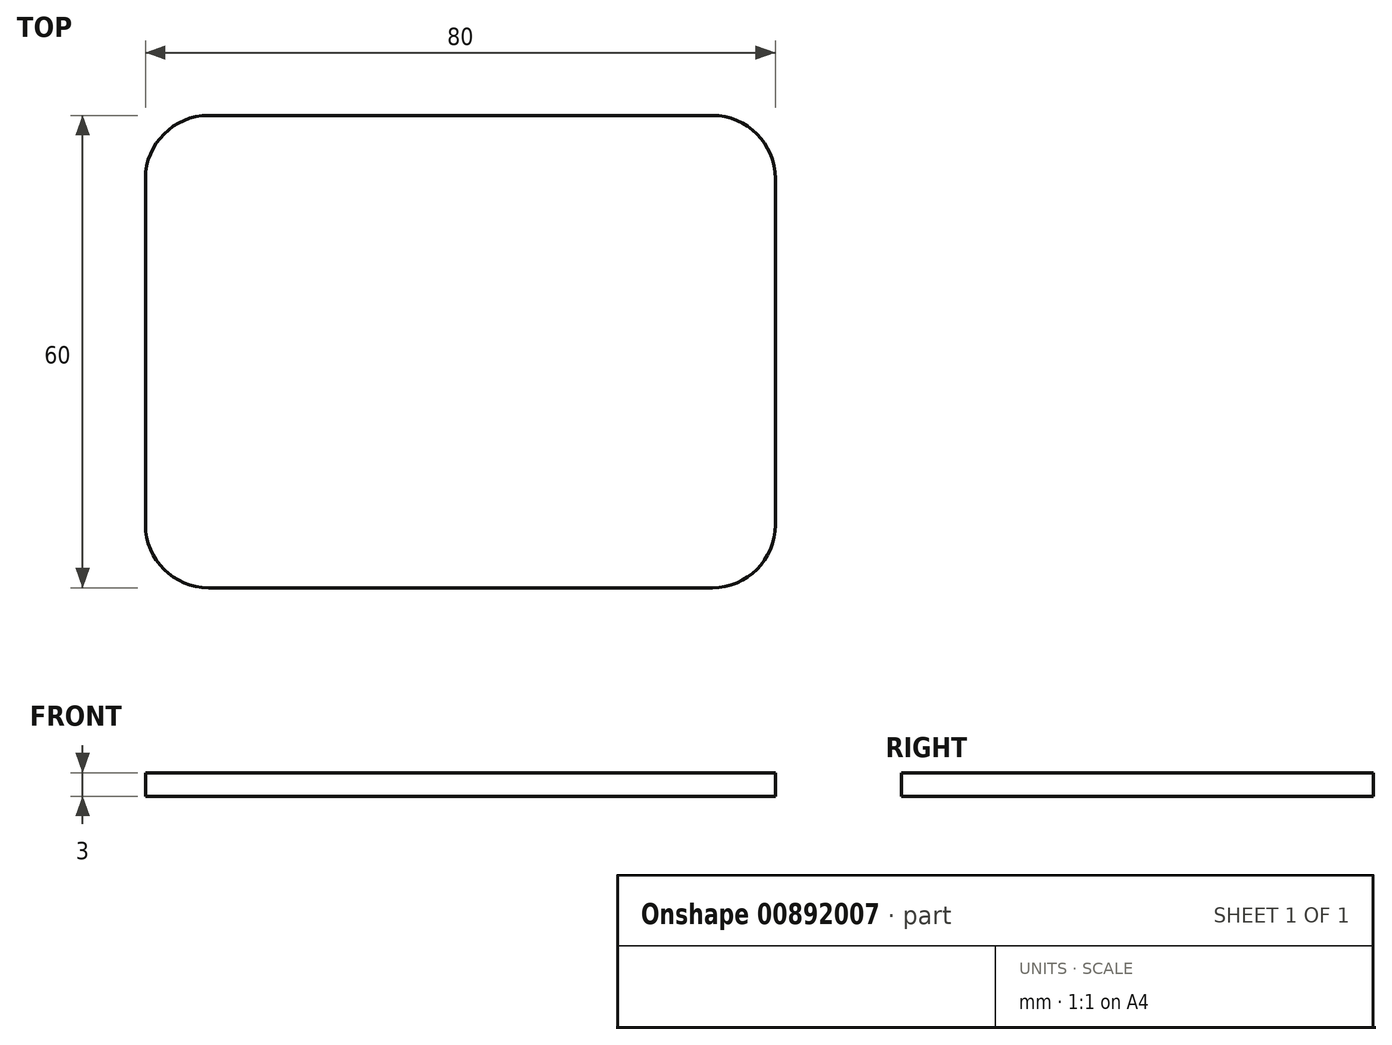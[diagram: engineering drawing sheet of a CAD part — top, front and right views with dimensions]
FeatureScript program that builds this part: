
annotation { "Feature Type Name" : "Feature", "Feature Type Description" : "" }
export const myFeature = defineFeature(function(context is Context, id is Id, definition is map)
    precondition{}
    {
        {
            var Q0;
            Q0=qCreatedBy(makeId("Top.planeOp"),FACE);
            var sketch = newSketch(context, id + "F0", { "sketchPlane" : qUnion([Q0])});
            skLineSegment(sketch, "E0.bottom", {"start": v(-32, 30) * mm, "end": v(32, 30) * mm});
            skLineSegment(sketch, "E0.top", {"start": v(-32, -30) * mm, "end": v(32, -30) * mm});
            skLineSegment(sketch, "E0.left", {"start": v(-40, 22) * mm, "end": v(-40, -22) * mm});
            skLineSegment(sketch, "E0.right", {"start": v(40, 22) * mm, "end": v(40, -22) * mm});
            skPoint(sketch, "E1.visualSharp", {"position": v(-40, 30) * mm});
            skArc(sketch, "E1.filletArc", {"start": v(-32, 30) * mm, "mid": v(-37.66, 27.66) * mm, "end": v(-40, 22) * mm});
            skPoint(sketch, "E2.visualSharp", {"position": v(40, 30) * mm});
            skArc(sketch, "E2.filletArc", {"start": v(40, 22) * mm, "mid": v(37.66, 27.66) * mm, "end": v(32, 30) * mm});
            skPoint(sketch, "E3.visualSharp", {"position": v(40, -30) * mm});
            skArc(sketch, "E3.filletArc", {"start": v(32, -30) * mm, "mid": v(37.66, -27.66) * mm, "end": v(40, -22) * mm});
            skPoint(sketch, "E4.visualSharp", {"position": v(-40, -30) * mm});
            skArc(sketch, "E4.filletArc", {"start": v(-40, -22) * mm, "mid": v(-37.66, -27.66) * mm, "end": v(-32, -30) * mm});
            skSolve(sketch);
        }
        {
            var Q0;
            Q0 = qSketchRegion(id + "F0", true);
            var Q1;
            Q1=makeQuery(id+"F0.imprint","IMPRINT",FACE,{"disambiguationData":[TD([[makeQuery(id+"F0.imprint","IMPRINT",EDGE,{"derivedFrom":sQuery(id+"F0.wireOp",EDGE,"E0.bottom")}),-1.0]])]});
            extrude(context, id + "F1", {"entities" : qUnion([Q0, Q1]), "depth" : 3 * mm, "offsetDistance" : 25 * mm});
        }
    });
